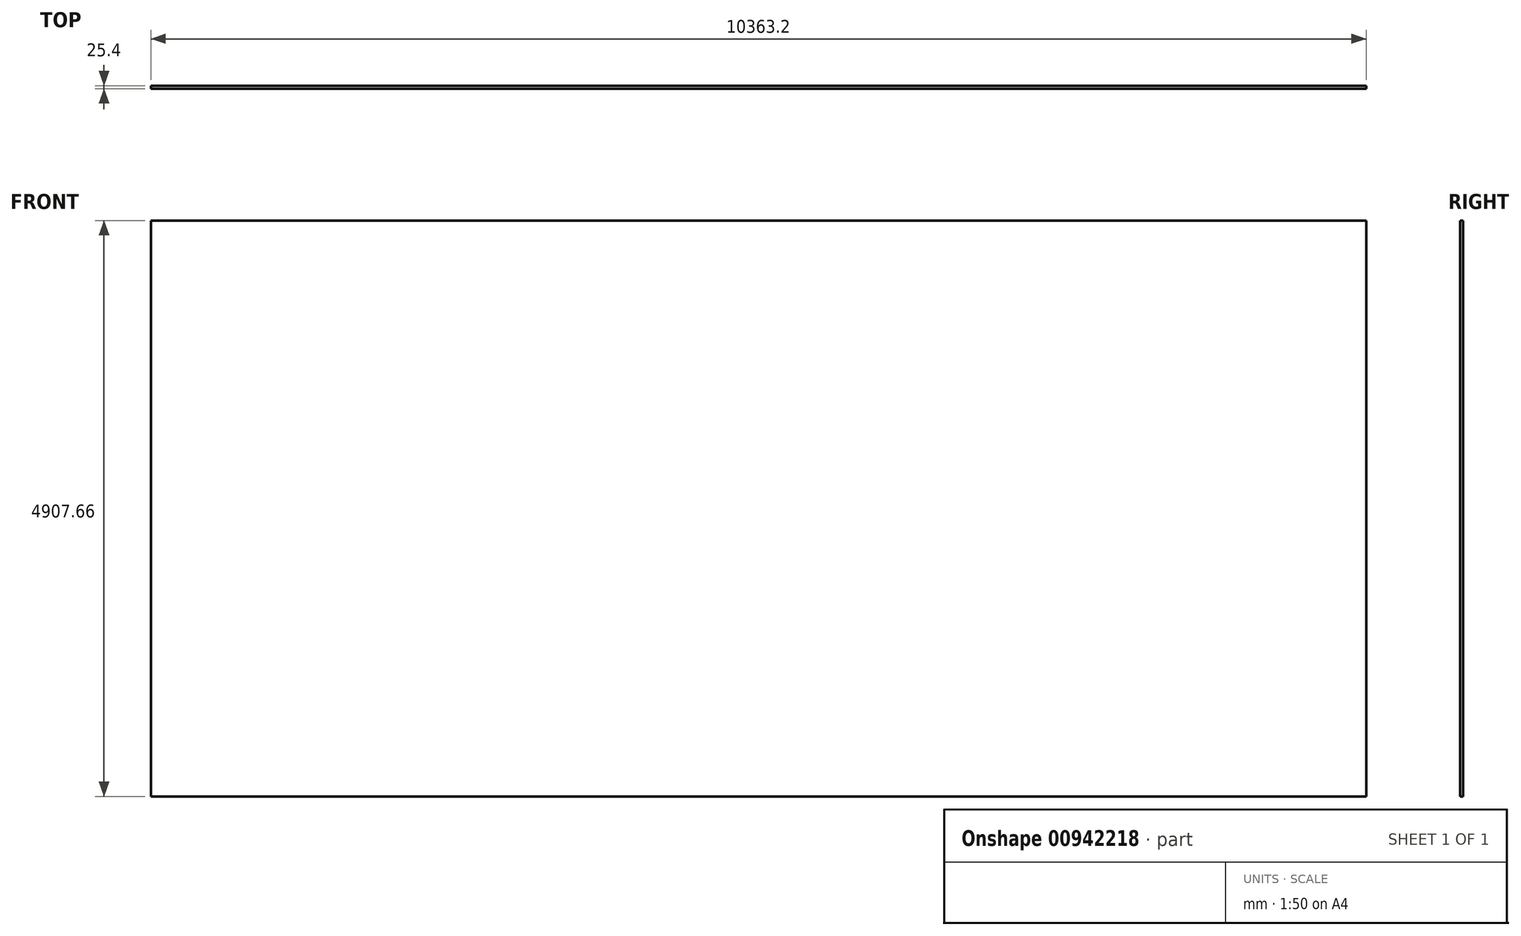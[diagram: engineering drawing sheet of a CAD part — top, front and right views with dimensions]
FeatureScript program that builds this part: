
annotation { "Feature Type Name" : "Feature", "Feature Type Description" : "" }
export const myFeature = defineFeature(function(context is Context, id is Id, definition is map)
    precondition{}
    {
        {
            var Q0;
            Q0=qCreatedBy(makeId("Front.planeOp"),FACE);
            var sketch = newSketch(context, id + "F0", { "sketchPlane" : qUnion([Q0])});
            skLineSegment(sketch, "E0.bottom", {"start": v(0, 0) * mm, "end": v(10363.2, 0) * mm});
            skLineSegment(sketch, "E0.top", {"start": v(0, 4907.66) * mm, "end": v(10363.2, 4907.66) * mm});
            skLineSegment(sketch, "E0.left", {"start": v(0, 0) * mm, "end": v(0, 4907.66) * mm});
            skLineSegment(sketch, "E0.right", {"start": v(10363.2, 0) * mm, "end": v(10363.2, 4907.66) * mm});
            skSolve(sketch);
        }
        {
            var Q0;
            Q0=makeQuery(id+"F0.imprint","IMPRINT",FACE,{"disambiguationData":[TD([[makeQuery(id+"F0.imprint","IMPRINT",EDGE,{"derivedFrom":sQuery(id+"F0.wireOp",EDGE,"E0.bottom")}),1.0]])]});
            extrude(context, id + "F1", {"entities" : qUnion([Q0]), "oppositeDirection" : true, "depth" : 25.4 * mm, "offsetDistance" : 25.4 * mm});
        }
    });
